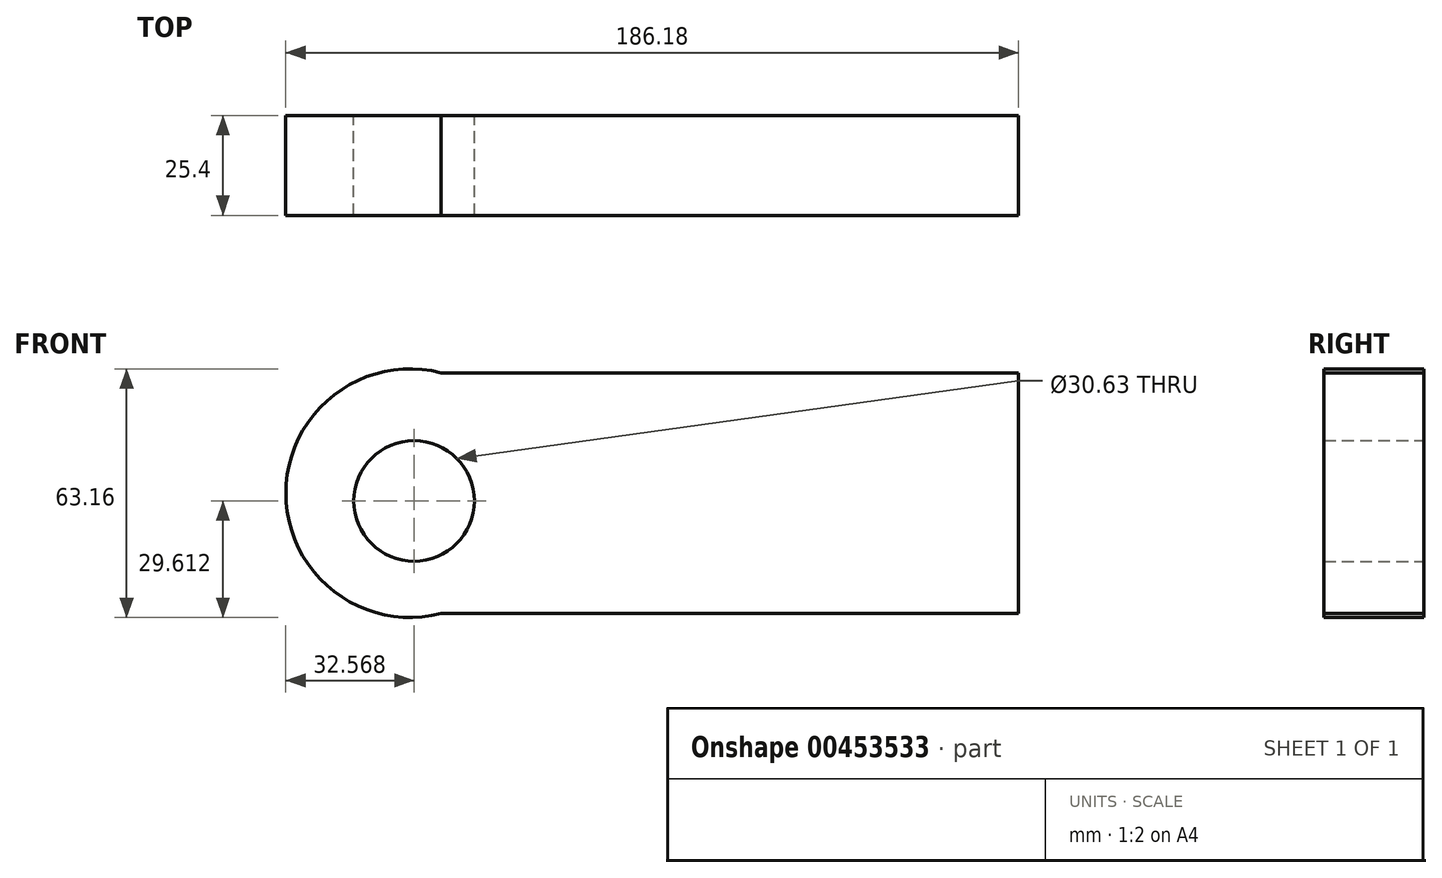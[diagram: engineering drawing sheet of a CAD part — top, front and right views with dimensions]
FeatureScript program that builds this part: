
annotation { "Feature Type Name" : "Feature", "Feature Type Description" : "" }
export const myFeature = defineFeature(function(context is Context, id is Id, definition is map)
    precondition{}
    {
        {
            var Q0;
            Q0=qCreatedBy(makeId("Front.planeOp"),FACE);
            var sketch = newSketch(context, id + "F0", { "sketchPlane" : qUnion([Q0])});
            skLineSegment(sketch, "E0.bottom", {"start": v(75.99, 30.6) * mm, "end": v(-75.99, 30.6) * mm});
            skLineSegment(sketch, "E0.top", {"start": v(75.99, -30.6) * mm, "end": v(-75.99, -30.6) * mm});
            skLineSegment(sketch, "E0.left", {"start": v(75.99, 30.6) * mm, "end": v(75.99, -30.6) * mm});
            skLineSegment(sketch, "E0.right", {"start": v(-75.99, 30.6) * mm, "end": v(-75.99, -30.6) * mm});
            skPoint(sketch, "E0.middle", {"position": v(0, 0) * mm});
            skCircle(sketch, "E1", {"center": v(-75.99, 0) * mm, "radius": 2.62 * mm});
            skCircle(sketch, "E2", {"center": v(-78.6, 0) * mm, "radius": 31.58 * mm});
            skCircle(sketch, "E3", {"center": v(-77.62, -1.97) * mm, "radius": 15.31 * mm});
            skSolve(sketch);
        }
        {
            var Q0;
            {var subQ0=sQuery(id+"F0.wireOp",EDGE,"E0.left");Q0=makeQuery(id+"F0.imprint","IMPRINT",FACE,{"disambiguationData":[TD([[makeQuery(id+"F0.imprint","IMPRINT",EDGE,{"derivedFrom":subQ0}),-1.0]])]});}
            extrude(context, id + "F1", {"entities" : qUnion([Q0]), "depth" : 25.4 * mm});
        }
        {
            var Q0;
            Q0=qCreatedBy(makeId("Front.planeOp"),FACE);
            var sketch = newSketch(context, id + "F2", { "sketchPlane" : qUnion([Q0])});
            skSolve(sketch);
        }
        {
            var Q0;
            Q0 = qSketchRegion(id + "F2", true);
            var Q1;
            Q1 = qSketchRegion(id + "F0", true);
            var Q2;
            {var subQ0=sQuery(id+"F0.wireOp",EDGE,"E0.right");var subQ5=sQuery(id+"F0.wireOp",EDGE,"E0.bottom");var subQ6=makeQuery(id+"F0.imprint","INTERSECT",VERTEX,{"derivedFrom":[subQ5,subQ0]});Q2=makeQuery(id+"F0.imprint","IMPRINT",FACE,{"disambiguationData":[TD([[makeQuery(id+"F0.imprint","IMPRINT",EDGE,{"disambiguationData":[TD([[subQ6,1.0]])],"derivedFrom":subQ5}),-1.0]])]});}
            var Q3;
            Q3 = qSketchRegion(id + "FdNHDMlbUN7ugmA_0", true);
            extrude(context, id + "F3", {"entities" : qUnion([Q0, Q1, Q2, Q3]), "operationType" : NewBodyOperationType.ADD, "depth" : 25.4 * mm});
        }
    });
